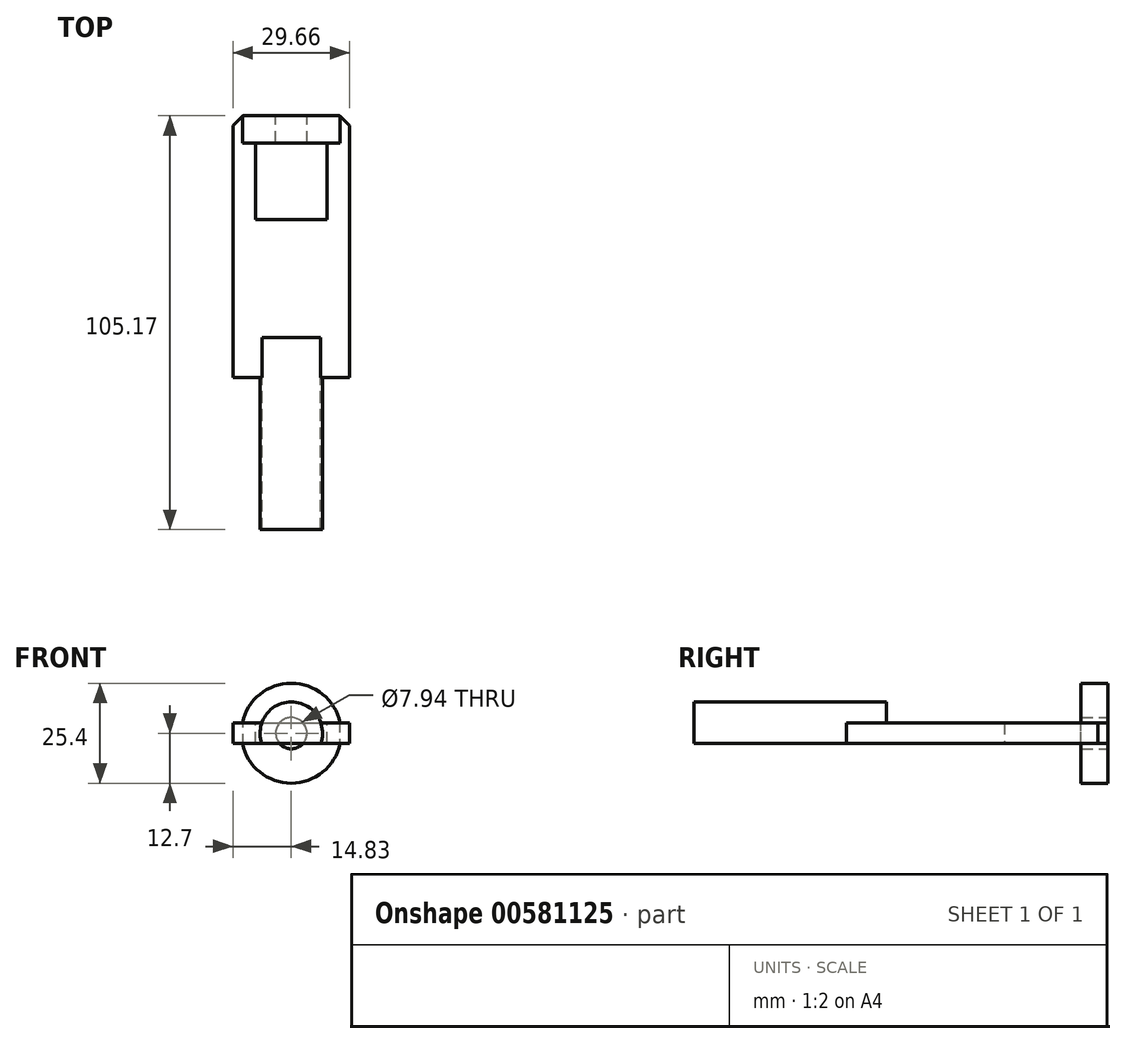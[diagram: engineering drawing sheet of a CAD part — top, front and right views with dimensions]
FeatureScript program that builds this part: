
annotation { "Feature Type Name" : "Feature", "Feature Type Description" : "" }
export const myFeature = defineFeature(function(context is Context, id is Id, definition is map)
    precondition{}
    {
        {
            var Q0;
            Q0=qCreatedBy(makeId("Front.planeOp"),FACE);
            var sketch = newSketch(context, id + "F0", { "sketchPlane" : qUnion([Q0])});
            skCircle(sketch, "E0", {"center": v(0, 0) * mm, "radius": 12.7 * mm});
            skCircle(sketch, "E1", {"center": v(0, 0) * mm, "radius": 3.97 * mm});
            skSolve(sketch);
        }
        {
            var Q0;
            Q0=makeQuery(id+"F0.imprint","IMPRINT",FACE,{"disambiguationData":[TD([[makeQuery(id+"F0.imprint","IMPRINT",EDGE,{"derivedFrom":sQuery(id+"F0.wireOp",EDGE,"E0")}),1.0]])]});
            extrude(context, id + "F1", {"entities" : qUnion([Q0]), "depth" : 6.88 * mm, "offsetDistance" : 25.4 * mm});
        }
        {
            var Q0;
            Q0=qCreatedBy(makeId("Top.planeOp"),FACE);
            var sketch = newSketch(context, id + "F2", { "sketchPlane" : qUnion([Q0])});
            skLineSegment(sketch, "E2.bottom", {"start": v(-14.83, 0) * mm, "end": v(-9.13, 0) * mm});
            skLineSegment(sketch, "E2.top", {"start": v(-14.83, -66.48) * mm, "end": v(14.83, -66.48) * mm});
            skLineSegment(sketch, "E2.left", {"start": v(-14.83, 0) * mm, "end": v(-14.83, -66.48) * mm});
            skLineSegment(sketch, "E2.right", {"start": v(14.83, 0) * mm, "end": v(14.83, -66.48) * mm});
            skLineSegment(sketch, "E3.top", {"start": v(-9.13, -26.34) * mm, "end": v(9.13, -26.34) * mm});
            skLineSegment(sketch, "E3.left", {"start": v(-9.13, 0) * mm, "end": v(-9.13, -26.34) * mm});
            skLineSegment(sketch, "E3.right", {"start": v(9.13, 0) * mm, "end": v(9.13, -26.34) * mm});
            skLineSegment(sketch, "E4.trimOffspring", {"start": v(9.13, 0) * mm, "end": v(14.83, 0) * mm});
            skSolve(sketch);
        }
        {
            var Q0;
            Q0=makeQuery(id+"F2.imprint","IMPRINT",FACE,{"disambiguationData":[TD([[makeQuery(id+"F2.imprint","IMPRINT",EDGE,{"derivedFrom":sQuery(id+"F2.wireOp",EDGE,"E2.bottom")}),-1.0]])]});
            extrude(context, id + "F3", {"entities" : qUnion([Q0]), "operationType" : NewBodyOperationType.ADD, "endBound" : BoundingType.SYMMETRIC, "depth" : 5.3 * mm, "offsetDistance" : 25.4 * mm});
        }
        {
            var Q0;
            Q0=makeQuery(id+"F3.opExtrude","SWEPT_EDGE",EDGE,{"disambiguationData":[OSD([sQuery(id+"F2.wireOp",EDGE,"E2.right"),sQuery(id+"F2.wireOp",EDGE,"E4.trimOffspring")])]});
            var Q1;
            Q1=makeQuery(id+"F3.opExtrude","SWEPT_EDGE",EDGE,{"disambiguationData":[OSD([sQuery(id+"F2.wireOp",EDGE,"E2.bottom"),sQuery(id+"F2.wireOp",EDGE,"E2.left")])]});
            chamfer(context, id + "F4", {"entities" : qUnion([Q0, Q1]), "width" : 2.54 * mm, "tangentPropagation" : true});
        }
        {
            var Q0;
            Q0=makeQuery(id+"F3.opExtrude","SWEPT_FACE",FACE,{"disambiguationData":[OSD([sQuery(id+"F2.wireOp",EDGE,"E2.top")])]});
            var sketch = newSketch(context, id + "F5", { "sketchPlane" : qUnion([Q0])});
            skCircle(sketch, "E5", {"center": v(0, 0) * mm, "radius": 7.94 * mm});
            skSolve(sketch);
        }
        {
            var Q0;
            {var subQ0=sQuery(id+"F5.wireOp",EDGE,"E5");var subQ1=makeQuery(id+"F3.opExtrude","CAP_EDGE",EDGE,{"disambiguationData":[OSD([sQuery(id+"F2.wireOp",EDGE,"E2.top")])],"isStart":true});var subQ2=makeQuery(id+"F5.imprint","INTERSECT",VERTEX,{"disambiguationData":[OD(0.0)],"derivedFrom":[subQ1,subQ0]});Q0=makeQuery(id+"F5.imprint","IMPRINT",FACE,{"disambiguationData":[TD([[makeQuery(id+"F5.imprint","IMPRINT",EDGE,{"disambiguationData":[TD([[subQ2,-1.0]])],"derivedFrom":subQ0}),1.0]])]});}
            var Q1;
            {var subQ0=sQuery(id+"F5.wireOp",EDGE,"E5");var subQ1=sQuery(id+"F2.wireOp",EDGE,"E2.top");var subQ2=makeQuery(id+"F3.opExtrude","CAP_EDGE",EDGE,{"disambiguationData":[OSD([subQ1])],"isStart":false});var subQ3=makeQuery(id+"F5.imprint","INTERSECT",VERTEX,{"disambiguationData":[OD(0.0)],"derivedFrom":[subQ2,subQ0]});Q1=makeQuery(id+"F5.imprint","IMPRINT",FACE,{"disambiguationData":[TD([[makeQuery(id+"F5.imprint","IMPRINT",EDGE,{"disambiguationData":[TD([[subQ3,-1.0]])],"derivedFrom":subQ0}),1.0]])]});}
            var Q2;
            {var subQ0=sQuery(id+"F5.wireOp",EDGE,"E5");var subQ1=makeQuery(id+"F3.opExtrude","CAP_EDGE",EDGE,{"disambiguationData":[OSD([sQuery(id+"F2.wireOp",EDGE,"E2.top")])],"isStart":false});var subQ2=makeQuery(id+"F5.imprint","INTERSECT",VERTEX,{"disambiguationData":[OD(0.0)],"derivedFrom":[subQ1,subQ0]});Q2=makeQuery(id+"F5.imprint","IMPRINT",FACE,{"disambiguationData":[TD([[makeQuery(id+"F5.imprint","IMPRINT",EDGE,{"disambiguationData":[TD([[subQ2,1.0]])],"derivedFrom":subQ0}),1.0]])]});}
            extrude(context, id + "F6", {"entities" : qUnion([Q0, Q1, Q2]), "operationType" : NewBodyOperationType.ADD, "depth" : 38.68 * mm, "offsetDistance" : 25.4 * mm, "hasSecondDirection" : true, "secondDirectionOppositeDirection" : true, "secondDirectionDepth" : 10.16 * mm});
        }
    });
